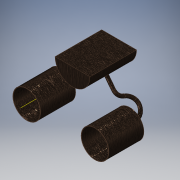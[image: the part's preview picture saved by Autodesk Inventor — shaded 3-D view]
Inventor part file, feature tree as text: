
AUTODESK INVENTOR PART (.ipt)
format: ipt  version: 2019 (Build 230136000, 136)  size: 232,960 bytes
history: native  units: mm
features: other x6, sketch x4, extrude x2, projected_geometry x2, sweep x1, mirror x1, shell x1
ambient origin geometry x8: Origin, YZ Plane, XZ Plane, XY Plane, X Axis, Y Axis, Z Axis, Center Point
bodies: Body1 (feature_tree)
feature tree (17):
  other  "Твердое тело1"
  extrude  "Выдавливание1"  Depth=150.0mm
  other  "РабПлоскость1"
  other  "Разделение1"
  other  "РабПлоскость2"
  extrude  "Выдавливание2"  Depth=200.0mm TaperAngle=0.0deg
  other  "РабОсь1"
  other  "РабПлоскость3"
  sweep  "Сдвиг1"
  mirror  "Зеркальное отражение1"
  shell  "Оболочка2"  Thickness=120.0mm
  sketch  "Эскиз1"
  sketch  "Эскиз2"
  sketch  "Эскиз3"
  projected_geometry  "Спроецированная петля1"
  projected_geometry  "Спроецированная петля2"
  sketch  "Эскиз4"
